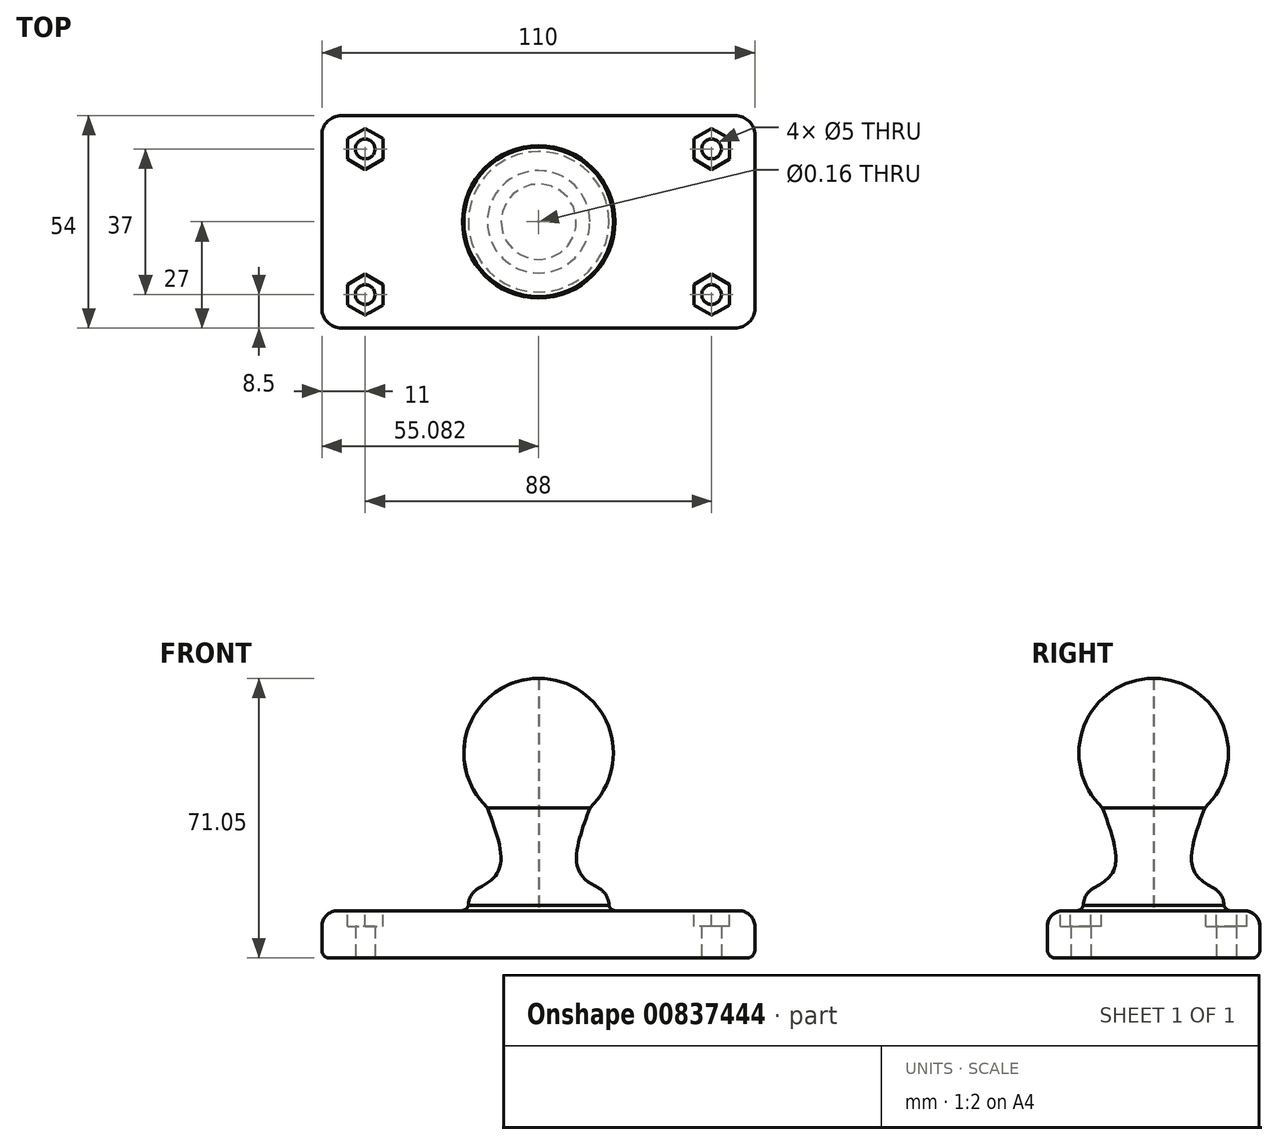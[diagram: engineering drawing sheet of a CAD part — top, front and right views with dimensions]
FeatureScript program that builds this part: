
annotation { "Feature Type Name" : "Feature", "Feature Type Description" : "" }
export const myFeature = defineFeature(function(context is Context, id is Id, definition is map)
    precondition{}
    {
        {
            var Q0;
            Q0=qCreatedBy(makeId("Top.planeOp"),FACE);
            var sketch = newSketch(context, id + "F0", { "sketchPlane" : qUnion([Q0])});
            skPoint(sketch, "E0.middle", {"position": v(0, 0) * mm});
            skCircle(sketch, "E1", {"center": v(-44, 18.5) * mm, "radius": 2.5 * mm});
            skCircle(sketch, "E2", {"center": v(44, 18.5) * mm, "radius": 2.5 * mm});
            skCircle(sketch, "E3", {"center": v(44, -18.5) * mm, "radius": 2.5 * mm});
            skCircle(sketch, "E4", {"center": v(-44, -18.5) * mm, "radius": 2.5 * mm});
            skLineSegment(sketch, "E5.bottom", {"start": v(50, 27) * mm, "end": v(-50, 27) * mm});
            skLineSegment(sketch, "E5.top", {"start": v(50, -27) * mm, "end": v(-50, -27) * mm});
            skLineSegment(sketch, "E5.left", {"start": v(55, 22) * mm, "end": v(55, -22) * mm});
            skLineSegment(sketch, "E5.right", {"start": v(-55, 22) * mm, "end": v(-55, -22) * mm});
            skPoint(sketch, "E6.visualSharp", {"position": v(-55, 27) * mm});
            skArc(sketch, "E6.filletArc", {"start": v(-50, 27) * mm, "mid": v(-53.54, 25.54) * mm, "end": v(-55, 22) * mm});
            skPoint(sketch, "E7.visualSharp", {"position": v(55, 27) * mm});
            skArc(sketch, "E7.filletArc", {"start": v(55, 22) * mm, "mid": v(53.54, 25.54) * mm, "end": v(50, 27) * mm});
            skPoint(sketch, "E8.visualSharp", {"position": v(55, -27) * mm});
            skArc(sketch, "E8.filletArc", {"start": v(50, -27) * mm, "mid": v(53.54, -25.54) * mm, "end": v(55, -22) * mm});
            skPoint(sketch, "E9.visualSharp", {"position": v(-55, -27) * mm});
            skArc(sketch, "E9.filletArc", {"start": v(-55, -22) * mm, "mid": v(-53.54, -25.54) * mm, "end": v(-50, -27) * mm});
            skSolve(sketch);
        }
        {
            var Q0;
            Q0=makeQuery(id+"F0.imprint","IMPRINT",FACE,{"disambiguationData":[TD([[makeQuery(id+"F0.imprint","IMPRINT",EDGE,{"derivedFrom":sQuery(id+"F0.wireOp",EDGE,"E1")}),-1.0]])]});
            extrude(context, id + "F1", {"entities" : qUnion([Q0]), "depth" : 12 * mm, "offsetDistance" : 25 * mm});
        }
        {
            var Q0;
            Q0=makeQuery(id+"F1.opExtrude","CAP_FACE",FACE,{"disambiguationData":[OSD([sQuery(id+"F0.wireOp",EDGE,"E1"),sQuery(id+"F0.wireOp",EDGE,"E2"),sQuery(id+"F0.wireOp",EDGE,"E3"),sQuery(id+"F0.wireOp",EDGE,"E4"),sQuery(id+"F0.wireOp",EDGE,"E5.bottom"),sQuery(id+"F0.wireOp",EDGE,"E5.top"),sQuery(id+"F0.wireOp",EDGE,"E5.left"),sQuery(id+"F0.wireOp",EDGE,"E5.right"),sQuery(id+"F0.wireOp",EDGE,"E6.filletArc"),sQuery(id+"F0.wireOp",EDGE,"E7.filletArc"),sQuery(id+"F0.wireOp",EDGE,"E8.filletArc"),sQuery(id+"F0.wireOp",EDGE,"E9.filletArc")])],"isStart":false});
            var sketch = newSketch(context, id + "F2", { "sketchPlane" : qUnion([Q0])});
            skCircle(sketch, "E10.cCircle", {"center": v(-44, 18.5) * mm, "radius": 4.5 * mm, "construction": true});
            skLineSegment(sketch, "E10.0", {"start": v(-39.5, 21.1) * mm, "end": v(-39.5, 15.9) * mm});
            skLineSegment(sketch, "E10.1", {"start": v(-39.5, 15.9) * mm, "end": v(-44, 13.3) * mm});
            skLineSegment(sketch, "E10.2", {"start": v(-44, 13.3) * mm, "end": v(-48.5, 15.9) * mm});
            skLineSegment(sketch, "E10.3", {"start": v(-48.5, 15.9) * mm, "end": v(-48.5, 21.1) * mm});
            skLineSegment(sketch, "E10.4", {"start": v(-48.5, 21.1) * mm, "end": v(-44, 23.7) * mm});
            skLineSegment(sketch, "E10.5", {"start": v(-44, 23.7) * mm, "end": v(-39.5, 21.1) * mm});
            skPoint(sketch, "E10.0.midPoint", {"position": v(-39.5, 18.5) * mm});
            skCircle(sketch, "E11.cCircle", {"center": v(44, 18.5) * mm, "radius": 4.5 * mm, "construction": true});
            skLineSegment(sketch, "E11.0", {"start": v(39.5, 15.9) * mm, "end": v(39.5, 21.1) * mm});
            skLineSegment(sketch, "E11.1", {"start": v(39.5, 21.1) * mm, "end": v(44, 23.7) * mm});
            skLineSegment(sketch, "E11.2", {"start": v(44, 23.7) * mm, "end": v(48.5, 21.1) * mm});
            skLineSegment(sketch, "E11.3", {"start": v(48.5, 21.1) * mm, "end": v(48.5, 15.9) * mm});
            skLineSegment(sketch, "E11.4", {"start": v(48.5, 15.9) * mm, "end": v(44, 13.3) * mm});
            skLineSegment(sketch, "E11.5", {"start": v(44, 13.3) * mm, "end": v(39.5, 15.9) * mm});
            skPoint(sketch, "E11.0.midPoint", {"position": v(39.5, 18.5) * mm});
            skCircle(sketch, "E12.cCircle", {"center": v(44, -18.5) * mm, "radius": 4.5 * mm, "construction": true});
            skLineSegment(sketch, "E12.0", {"start": v(39.5, -21.1) * mm, "end": v(39.5, -15.9) * mm});
            skLineSegment(sketch, "E12.1", {"start": v(39.5, -15.9) * mm, "end": v(44, -13.3) * mm});
            skLineSegment(sketch, "E12.2", {"start": v(44, -13.3) * mm, "end": v(48.5, -15.9) * mm});
            skLineSegment(sketch, "E12.3", {"start": v(48.5, -15.9) * mm, "end": v(48.5, -21.1) * mm});
            skLineSegment(sketch, "E12.4", {"start": v(48.5, -21.1) * mm, "end": v(44, -23.7) * mm});
            skLineSegment(sketch, "E12.5", {"start": v(44, -23.7) * mm, "end": v(39.5, -21.1) * mm});
            skPoint(sketch, "E12.0.midPoint", {"position": v(39.5, -18.5) * mm});
            skCircle(sketch, "E13.cCircle", {"center": v(-44, -18.5) * mm, "radius": 4.5 * mm, "construction": true});
            skLineSegment(sketch, "E13.0", {"start": v(-39.5, -15.9) * mm, "end": v(-39.5, -21.1) * mm});
            skLineSegment(sketch, "E13.1", {"start": v(-39.5, -21.1) * mm, "end": v(-44, -23.7) * mm});
            skLineSegment(sketch, "E13.2", {"start": v(-44, -23.7) * mm, "end": v(-48.5, -21.1) * mm});
            skLineSegment(sketch, "E13.3", {"start": v(-48.5, -21.1) * mm, "end": v(-48.5, -15.9) * mm});
            skLineSegment(sketch, "E13.4", {"start": v(-48.5, -15.9) * mm, "end": v(-44, -13.3) * mm});
            skLineSegment(sketch, "E13.5", {"start": v(-44, -13.3) * mm, "end": v(-39.5, -15.9) * mm});
            skPoint(sketch, "E13.0.midPoint", {"position": v(-39.5, -18.5) * mm});
            skSolve(sketch);
        }
        {
            var Q0;
            Q0=makeQuery(id+"F2.imprint","IMPRINT",FACE,{"disambiguationData":[TD([[makeQuery(id+"F2.imprint","IMPRINT",EDGE,{"derivedFrom":sQuery(id+"F2.wireOp",EDGE,"E10.0")}),-1.0]])]});
            var Q1;
            Q1=makeQuery(id+"F2.imprint","IMPRINT",FACE,{"disambiguationData":[TD([[makeQuery(id+"F2.imprint","IMPRINT",EDGE,{"derivedFrom":sQuery(id+"F2.wireOp",EDGE,"E11.0")}),-1.0]])]});
            var Q2;
            Q2=makeQuery(id+"F2.imprint","IMPRINT",FACE,{"disambiguationData":[TD([[makeQuery(id+"F2.imprint","IMPRINT",EDGE,{"derivedFrom":sQuery(id+"F2.wireOp",EDGE,"E12.0")}),-1.0]])]});
            var Q3;
            Q3=makeQuery(id+"F2.imprint","IMPRINT",FACE,{"disambiguationData":[TD([[makeQuery(id+"F2.imprint","IMPRINT",EDGE,{"derivedFrom":sQuery(id+"F2.wireOp",EDGE,"E13.0")}),-1.0]])]});
            extrude(context, id + "F3", {"entities" : qUnion([Q0, Q1, Q2, Q3]), "operationType" : NewBodyOperationType.REMOVE, "oppositeDirection" : true, "depth" : 4 * mm, "offsetDistance" : 25 * mm});
        }
        {
            var Q0;
            Q0=qCreatedBy(makeId("Front.planeOp"),FACE);
            var sketch = newSketch(context, id + "F4", { "sketchPlane" : qUnion([Q0])});
            skLineSegment(sketch, "E14", {"start": v(0, 0) * mm, "end": v(0, 105) * mm});
            skLineSegment(sketch, "E15", {"start": v(0.08, 12) * mm, "end": v(0.08, 70.56) * mm});
            skArc(sketch, "E16", {"start": v(0.08, 71.05) * mm, "mid": v(-17.58, 59.04) * mm, "end": v(-12.92, 38.2) * mm});
            skFitSpline(sketch, "E17", {"points": [v(-17.77, 16.48) * mm, v(-9.96, 22.54) * mm, v(-12.92, 38.2) * mm], "startDerivative": vector(22.8, 10.62) * mm, "endDerivative": vector(-11.71, 31.98) * mm});
            skArc(sketch, "E18.filletArc", {"start": v(-15.09, 17.78) * mm, "mid": v(-17.05, 15.94) * mm, "end": v(-17.77, 13.35) * mm});
            skFitSpline(sketch, "E19", {"points": [v(-17.77, 13.35) * mm, v(-18.3, 12.5) * mm, v(-19.3, 12) * mm], "startDerivative": vector(-0.86, -1.95) * mm, "endDerivative": vector(-2.17, -0.75) * mm});
            skLineSegment(sketch, "E20", {"start": v(-19.3, 12) * mm, "end": v(0.08, 12) * mm});
            skLineSegment(sketch, "E21", {"start": v(0.08, 12) * mm, "end": v(0.08, 78.54) * mm});
            skSolve(sketch);
        }
        {
            var Q0;
            {var subQ0=sQuery(id+"F4.wireOp",EDGE,"E17");Q0=makeQuery(id+"F4.imprint","IMPRINT",FACE,{"disambiguationData":[TD([[makeQuery(id+"F4.imprint","IMPRINT",EDGE,{"derivedFrom":subQ0}),-1.0]])]});}
            var Q1;
            Q1=sQuery(id+"F4.wireOp",EDGE,"E15");
            revolve(context, id + "F5", {"operationType" : NewBodyOperationType.ADD, "surfaceOperationType" : NewSurfaceOperationType.NEW, "entities" : qUnion([Q0]), "axis" : qUnion([Q1]), "revolveType" : RevolveType.FULL});
        }
        {
            var Q0;
            Q0=makeQuery(id+"F1.opExtrude","CAP_EDGE",EDGE,{"disambiguationData":[OSD([sQuery(id+"F0.wireOp",EDGE,"E5.bottom")])],"isStart":false});
            fillet(context, id + "F6", {"entities" : qUnion([Q0]), "radius" : 4 * mm, "tangentPropagation" : true, "allowEdgeOverflow" : false});
        }
        {
            var Q0;
            Q0=makeQuery(id+"F1.opExtrude","CAP_EDGE",EDGE,{"disambiguationData":[OSD([sQuery(id+"F0.wireOp",EDGE,"E5.bottom")])],"isStart":true});
            fillet(context, id + "F7", {"entities" : qUnion([Q0]), "radius" : 2 * mm, "tangentPropagation" : true, "allowEdgeOverflow" : false});
        }
    });
